# Revit family: Wenger Cabinet 13
name_source: partatom
category: Furniture
revit_build: Autodesk Revit Architecture 2012 (Build: 20110916_2132(x64)
units: mm (PartAtom-declared; Revit-internal decimal feet)

## types (4) — shared parameters
Cabinet Height = 7' - 1 5/8"
Manufacturer = Wenger Corporation
URL = http://www.wengercorp.com

## per-type parameters (varying)
| type | Cabinet Back Thickness | Cabinet Depth | Cabinet Label | Cabinet Width | Model |
| Standard Cabinet #13 | 0' - 0 3/4" | 2' - 5 1/4" | Labels : Standard | 1' - 2 3/8" | 13 |
| Acoustic Cabinet #13 | 0' - 3 1/4" | 2' - 7 3/4" | Labels : Acoustic | 1' - 2 3/8" | 13A |
| Narrow Acoustic Cabinet #13 | 0' - 3 1/4" | 2' - 7 3/4" | Labels : Narrow Acoustic | 0' - 11 3/8" | 13NA |
| Narrow Cabinet #13 | 0' - 0 3/4" | 2' - 5 1/4" | Labels : Narrow | 0' - 11 3/8" | 13N |

note: column(s) folded — value = type name in every type: Description

## geometry (parser evidence)
native form markers: Blend x22, Sweep x6
no freeform markers — native parametric forms only
